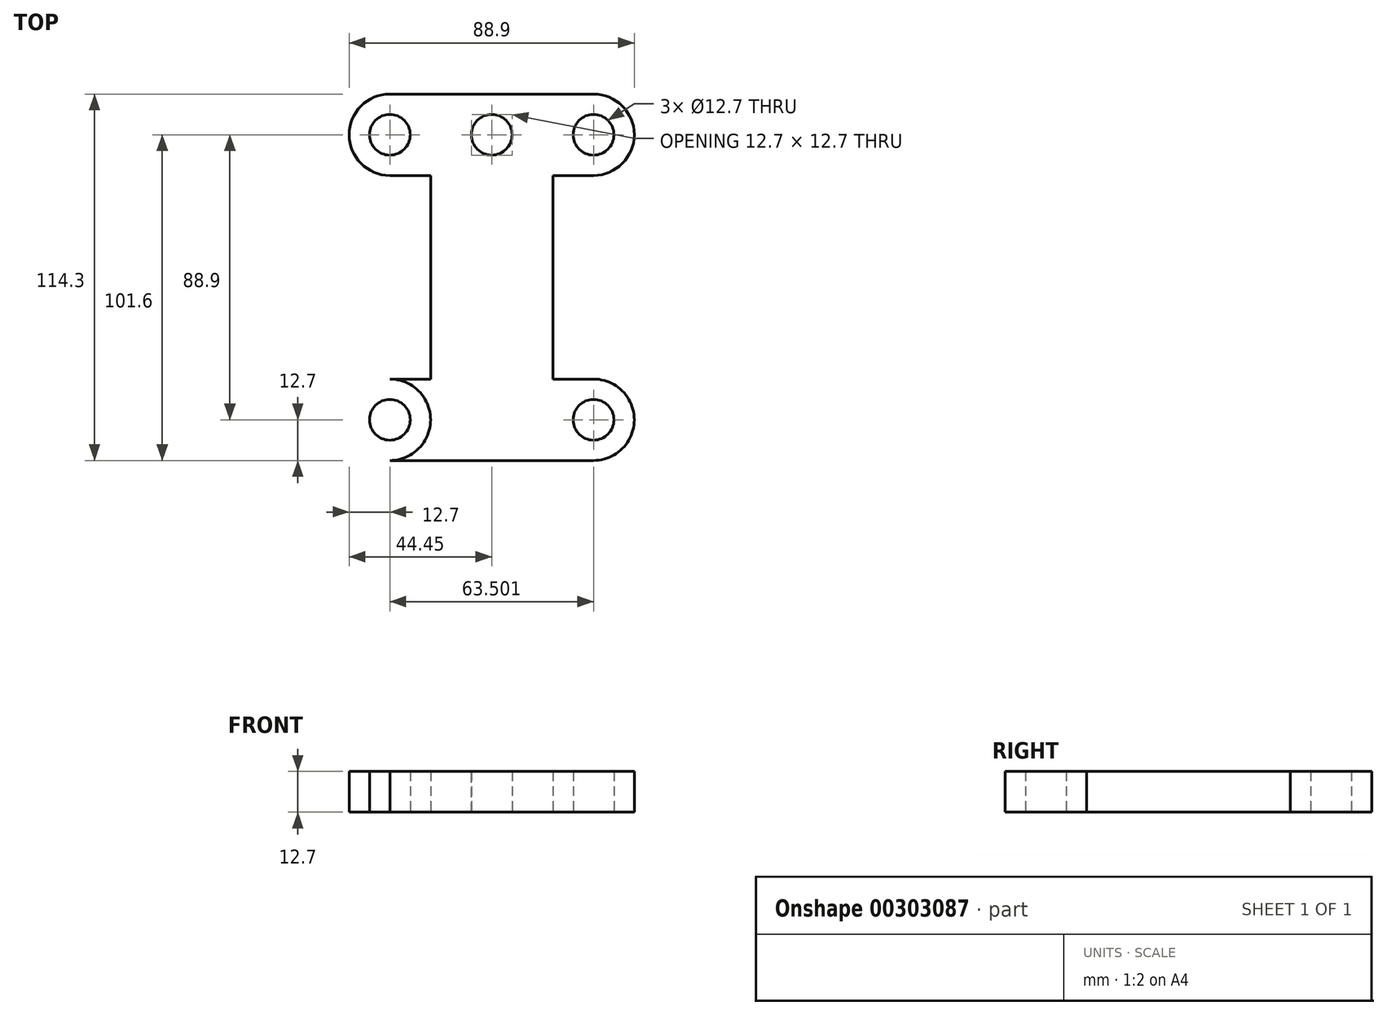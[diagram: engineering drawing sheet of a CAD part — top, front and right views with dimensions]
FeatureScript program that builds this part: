
annotation { "Feature Type Name" : "Feature", "Feature Type Description" : "" }
export const myFeature = defineFeature(function(context is Context, id is Id, definition is map)
    precondition{}
    {
        {
            var Q0;
            Q0=qCreatedBy(makeId("Top.planeOp"),FACE);
            var sketch = newSketch(context, id + "F0", { "sketchPlane" : qUnion([Q0])});
            skLineSegment(sketch, "E0", {"start": v(0, 0) * mm, "end": v(-31.75, 0) * mm});
            skLineSegment(sketch, "E1", {"start": v(0, 0) * mm, "end": v(31.75, 0) * mm});
            skCircle(sketch, "E2", {"center": v(-31.75, 12.7) * mm, "radius": 12.7 * mm});
            skCircle(sketch, "E3", {"center": v(31.75, 12.7) * mm, "radius": 12.7 * mm});
            skLineSegment(sketch, "E4", {"start": v(-31.75, 25.4) * mm, "end": v(-19.05, 25.4) * mm});
            skLineSegment(sketch, "E5", {"start": v(19.05, 12.7) * mm, "end": v(19.05, 12.7) * mm});
            skLineSegment(sketch, "E6", {"start": v(-19.05, 25.4) * mm, "end": v(-19.05, 88.9) * mm});
            skLineSegment(sketch, "E7", {"start": v(19.05, 25.4) * mm, "end": v(19.05, 88.9) * mm});
            skCircle(sketch, "E8", {"center": v(31.75, 12.7) * mm, "radius": 6.35 * mm});
            skCircle(sketch, "E9", {"center": v(-31.75, 12.7) * mm, "radius": 6.35 * mm});
            skCircle(sketch, "E10", {"center": v(-31.75, 101.6) * mm, "radius": 12.7 * mm});
            skCircle(sketch, "E11", {"center": v(31.75, 101.6) * mm, "radius": 12.7 * mm});
            skCircle(sketch, "E12", {"center": v(31.75, 101.6) * mm, "radius": 6.35 * mm});
            skCircle(sketch, "E13", {"center": v(-31.75, 101.6) * mm, "radius": 6.35 * mm});
            skLineSegment(sketch, "E14", {"start": v(-31.75, 114.3) * mm, "end": v(31.75, 114.3) * mm});
            skLineSegment(sketch, "E15", {"start": v(-31.75, 88.9) * mm, "end": v(-19.05, 88.9) * mm});
            skPoint(sketch, "E16", {"position": v(0, 114.3) * mm});
            skPoint(sketch, "E17", {"position": v(-19.05, 88.9) * mm});
            skPoint(sketch, "E18", {"position": v(19.05, 88.9) * mm});
            skLineSegment(sketch, "E19.trimOffspring", {"start": v(19.05, 101.6) * mm, "end": v(19.05, 101.6) * mm});
            skLineSegment(sketch, "E20.trimOffspring", {"start": v(-19.05, 101.6) * mm, "end": v(-19.05, 101.61) * mm});
            skLineSegment(sketch, "E21.trimOffspring", {"start": v(19.05, 25.4) * mm, "end": v(31.75, 25.4) * mm});
            skLineSegment(sketch, "E22.trimOffspring", {"start": v(19.05, 88.9) * mm, "end": v(31.75, 88.9) * mm});
            skLineSegment(sketch, "E23", {"start": v(0, 114.3) * mm, "end": v(0, 101.6) * mm});
            skCircle(sketch, "E24", {"center": v(0, 101.6) * mm, "radius": 6.35 * mm});
            skLineSegment(sketch, "E25", {"start": v(6.35, 101.6) * mm, "end": v(6.35, 114.3) * mm});
            skLineSegment(sketch, "E26", {"start": v(-6.35, 114.3) * mm, "end": v(-6.35, 101.6) * mm});
            skSolve(sketch);
        }
        {
            var Q0;
            Q0 = qSketchRegion(id + "F0", true);
            extrude(context, id + "F1", {"entities" : qUnion([Q0]), "depth" : 12.7 * mm});
        }
    });
